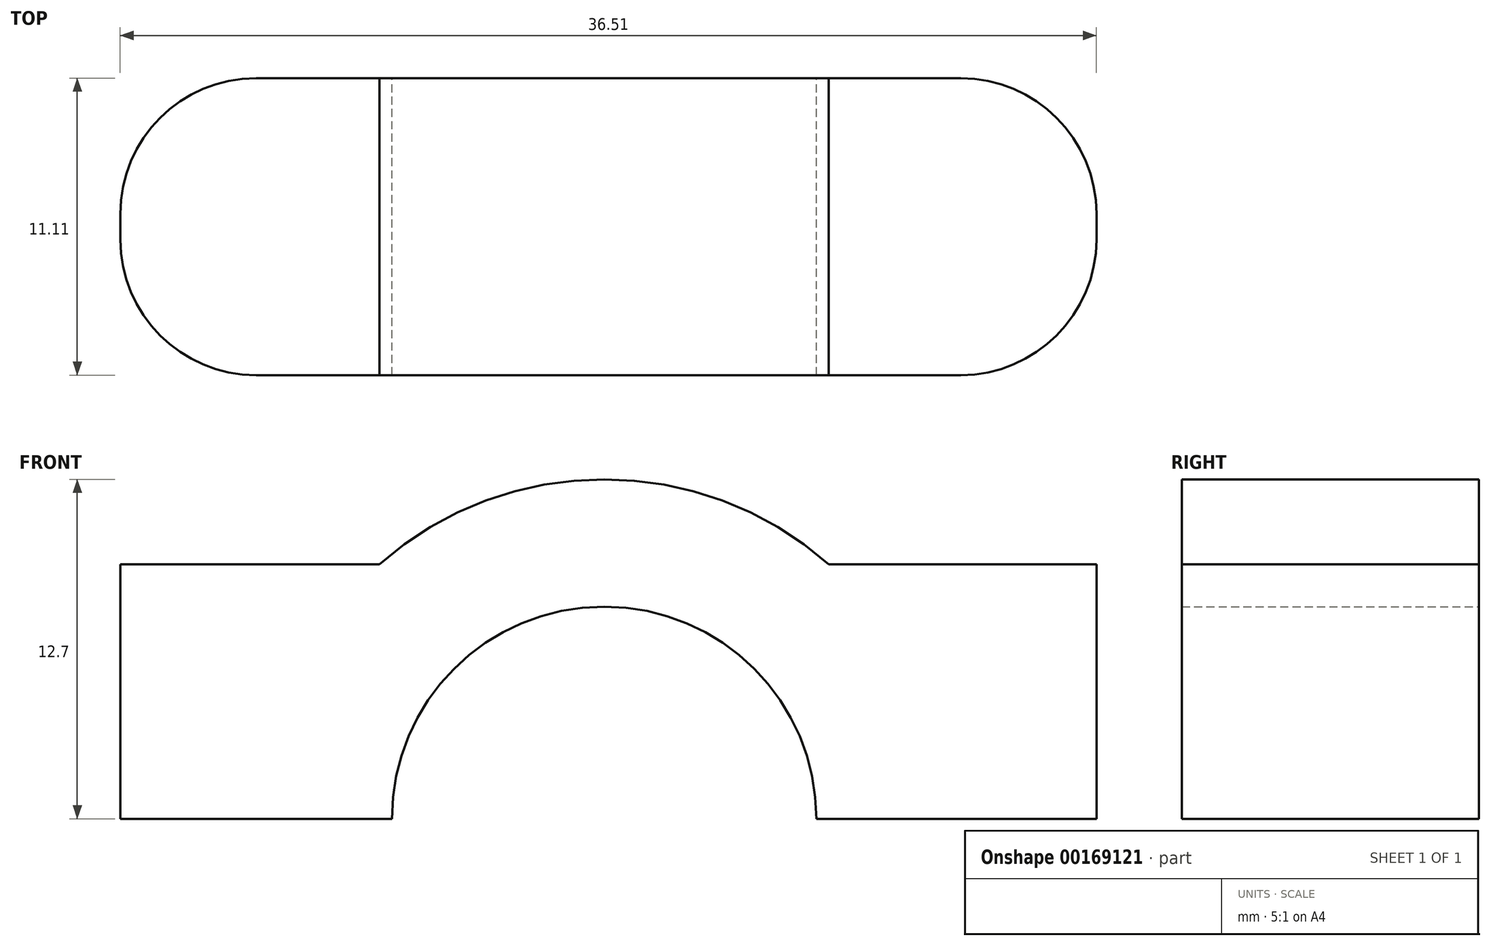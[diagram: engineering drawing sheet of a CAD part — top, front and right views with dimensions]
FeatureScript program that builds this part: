
annotation { "Feature Type Name" : "Feature", "Feature Type Description" : "" }
export const myFeature = defineFeature(function(context is Context, id is Id, definition is map)
    precondition{}
    {
        {
            var Q0;
            Q0=qCreatedBy(makeId("Front.planeOp"),FACE);
            var sketch = newSketch(context, id + "F0", { "sketchPlane" : qUnion([Q0])});
            skArc(sketch, "E0", {"start": v(7.94, 0) * mm, "mid": v(0, 7.94) * mm, "end": v(-7.94, 0) * mm});
            skLineSegment(sketch, "E1", {"start": v(-18.1, 0) * mm, "end": v(-18.1, 9.53) * mm});
            skLineSegment(sketch, "E2", {"start": v(-18.1, 9.53) * mm, "end": v(-8.4, 9.53) * mm});
            skLineSegment(sketch, "E3", {"start": v(18.41, 9.53) * mm, "end": v(18.41, 0) * mm});
            skLineSegment(sketch, "E4", {"start": v(18.41, 0) * mm, "end": v(7.94, 0) * mm});
            skLineSegment(sketch, "E5.trimOffspring", {"start": v(8.4, 9.53) * mm, "end": v(18.41, 9.53) * mm});
            skArc(sketch, "E6.trimOffspring", {"start": v(8.4, 9.52) * mm, "mid": v(0, 12.7) * mm, "end": v(-8.4, 9.53) * mm});
            skLineSegment(sketch, "E7.trimOffspring", {"start": v(-7.94, 0) * mm, "end": v(-18.1, 0) * mm});
            skSolve(sketch);
        }
        {
            var Q0;
            Q0=makeQuery(id+"F0.imprint","IMPRINT",FACE,{"disambiguationData":[TD([[makeQuery(id+"F0.imprint","IMPRINT",EDGE,{"derivedFrom":sQuery(id+"F0.wireOp",EDGE,"E0")}),-1.0]])]});
            extrude(context, id + "F1", {"entities" : qUnion([Q0]), "depth" : 11.1 * mm});
        }
        {
            var Q0;
            Q0=makeQuery(id+"F1.opExtrude","CAP_EDGE",EDGE,{"disambiguationData":[OSD([sQuery(id+"F0.wireOp",EDGE,"E1")])],"isStart":false});
            var Q1;
            Q1=makeQuery(id+"F1.opExtrude","CAP_EDGE",EDGE,{"disambiguationData":[OSD([sQuery(id+"F0.wireOp",EDGE,"E3")])],"isStart":false});
            var Q2;
            Q2=makeQuery(id+"F1.opExtrude","CAP_EDGE",EDGE,{"disambiguationData":[OSD([sQuery(id+"F0.wireOp",EDGE,"E3")])],"isStart":true});
            var Q3;
            Q3=makeQuery(id+"F1.opExtrude","CAP_EDGE",EDGE,{"disambiguationData":[OSD([sQuery(id+"F0.wireOp",EDGE,"E1")])],"isStart":true});
            fillet(context, id + "F2", {"entities" : qUnion([Q0, Q1, Q2, Q3]), "radius" : 5.08 * mm, "tangentPropagation" : true, "allowEdgeOverflow" : false});
        }
    });
